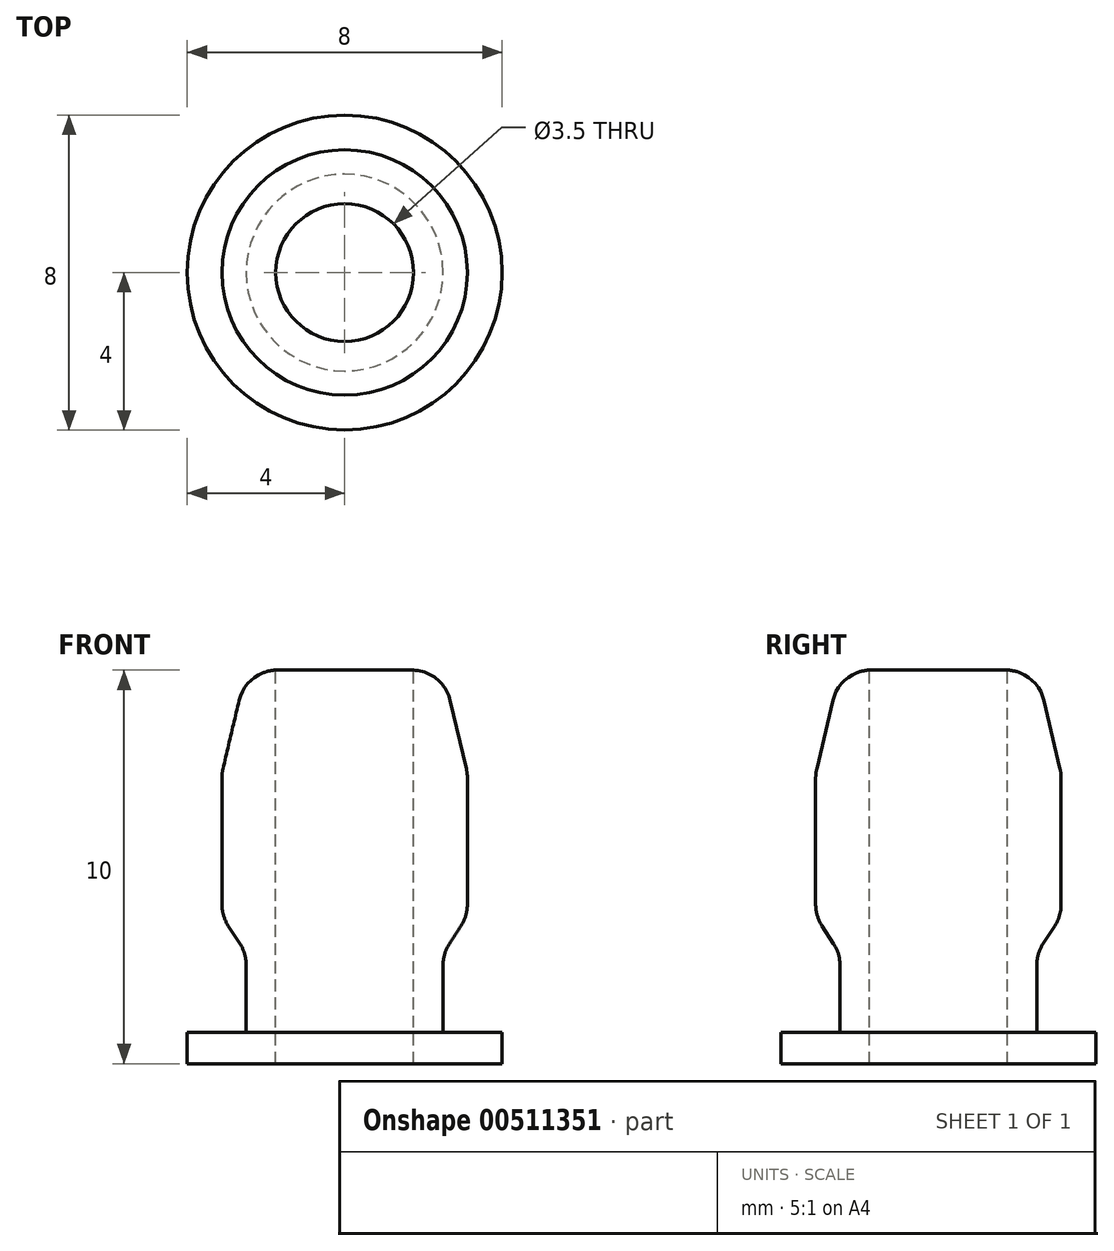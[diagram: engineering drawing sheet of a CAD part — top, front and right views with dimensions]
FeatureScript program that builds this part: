
annotation { "Feature Type Name" : "Feature", "Feature Type Description" : "" }
export const myFeature = defineFeature(function(context is Context, id is Id, definition is map)
    precondition{}
    {
        {
            var Q0;
            Q0=qCreatedBy(makeId("Front.planeOp"),FACE);
            var sketch = newSketch(context, id + "F0", { "sketchPlane" : qUnion([Q0])});
            skLineSegment(sketch, "E0", {"start": v(0, 0) * mm, "end": v(0, 10) * mm});
            skLineSegment(sketch, "E1", {"start": v(0, 0) * mm, "end": v(-4, 0) * mm});
            skLineSegment(sketch, "E2", {"start": v(-4, 0) * mm, "end": v(-4, 0.8) * mm});
            skLineSegment(sketch, "E3", {"start": v(-4, 0.8) * mm, "end": v(-2.5, 0.8) * mm});
            skLineSegment(sketch, "E4", {"start": v(-2.5, 0.8) * mm, "end": v(-2.5, 2.8) * mm});
            skLineSegment(sketch, "E5", {"start": v(-2.5, 2.8) * mm, "end": v(-3.12, 3.75) * mm});
            skLineSegment(sketch, "E6", {"start": v(-3.12, 3.75) * mm, "end": v(-3.12, 7.38) * mm});
            skLineSegment(sketch, "E7", {"start": v(-2.5, 10) * mm, "end": v(-3.12, 7.38) * mm});
            skLineSegment(sketch, "E8", {"start": v(-2.5, 10) * mm, "end": v(0, 10) * mm});
            skSolve(sketch);
        }
        {
            var Q0;
            Q0=makeQuery(id+"F0.imprint","IMPRINT",FACE,{"disambiguationData":[TD([[makeQuery(id+"F0.imprint","IMPRINT",EDGE,{"derivedFrom":sQuery(id+"F0.wireOp",EDGE,"E0")}),1.0]])]});
            var Q1;
            Q1=sQuery(id+"F0.wireOp",EDGE,"E0");
            revolve(context, id + "F1", {"entities" : qUnion([Q0]), "axis" : qUnion([Q1]), "revolveType" : RevolveType.FULL});
        }
        {
            var Q0;
            Q0=makeQuery(id+"F1.opRevolve","SWEPT_FACE",FACE,{"disambiguationData":[OSD([sQuery(id+"F0.wireOp",EDGE,"E8")])]});
            var sketch = newSketch(context, id + "F2", { "sketchPlane" : qUnion([Q0])});
            skCircle(sketch, "E9", {"center": v(0, 0) * mm, "radius": 1.75 * mm});
            skSolve(sketch);
        }
        {
            var Q0;
            Q0=makeQuery(id+"F2.imprint","IMPRINT",FACE,{"disambiguationData":[TD([[makeQuery(id+"F2.imprint","IMPRINT",EDGE,{"derivedFrom":sQuery(id+"F2.wireOp",EDGE,"E9")}),1.0]])]});
            var Q1;
            Q1=makeQuery(id+"F1.opRevolve","SWEPT_FACE",FACE,{"disambiguationData":[OSD([sQuery(id+"F0.wireOp",EDGE,"E3")])]});
            extrude(context, id + "F3", {"entities" : qUnion([Q0]), "operationType" : NewBodyOperationType.REMOVE, "oppositeDirection" : true, "endBoundEntityFace" : qUnion([Q1]), "depth" : 25 * mm});
        }
        {
            var Q0;
            Q0=makeQuery(id+"F1.opRevolve","SWEPT_FACE",FACE,{"disambiguationData":[OSD([sQuery(id+"F0.wireOp",EDGE,"E7")])]});
            var Q1;
            Q1=makeQuery(id+"F1.opRevolve","SWEPT_FACE",FACE,{"disambiguationData":[OSD([sQuery(id+"F0.wireOp",EDGE,"E6")])]});
            var Q2;
            Q2=makeQuery(id+"F1.opRevolve","SWEPT_FACE",FACE,{"disambiguationData":[OSD([sQuery(id+"F0.wireOp",EDGE,"E5")])]});
            fillet(context, id + "F4", {"entities" : qUnion([Q0, Q1, Q2]), "radius" : 1 * mm, "tangentPropagation" : true, "allowEdgeOverflow" : false});
        }
    });
